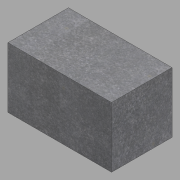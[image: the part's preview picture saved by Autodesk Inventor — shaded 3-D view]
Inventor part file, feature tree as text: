
AUTODESK INVENTOR PART (.ipt)
format: ipt  version: 2022.1 (Build 261234020, 234B)  size: 127,488 bytes
history: native  units: in
note: dims shown in document units (in); Inventor stores cm internally (conversion verified against a paired STEP export)
features: other x1, extrude x1, sketch x1
ambient origin geometry x8: Origin, YZ Plane, XZ Plane, XY Plane, X Axis, Y Axis, Z Axis, Center Point
bodies: Solid1 (feature_tree)
feature tree (3):
  other  "1st"
  extrude  "Extrusion1"  Depth=35.0in
  sketch  "Sketch1"  dims[d0=60.0in d1=35.0in d2=35.0in d3=0.0in]
